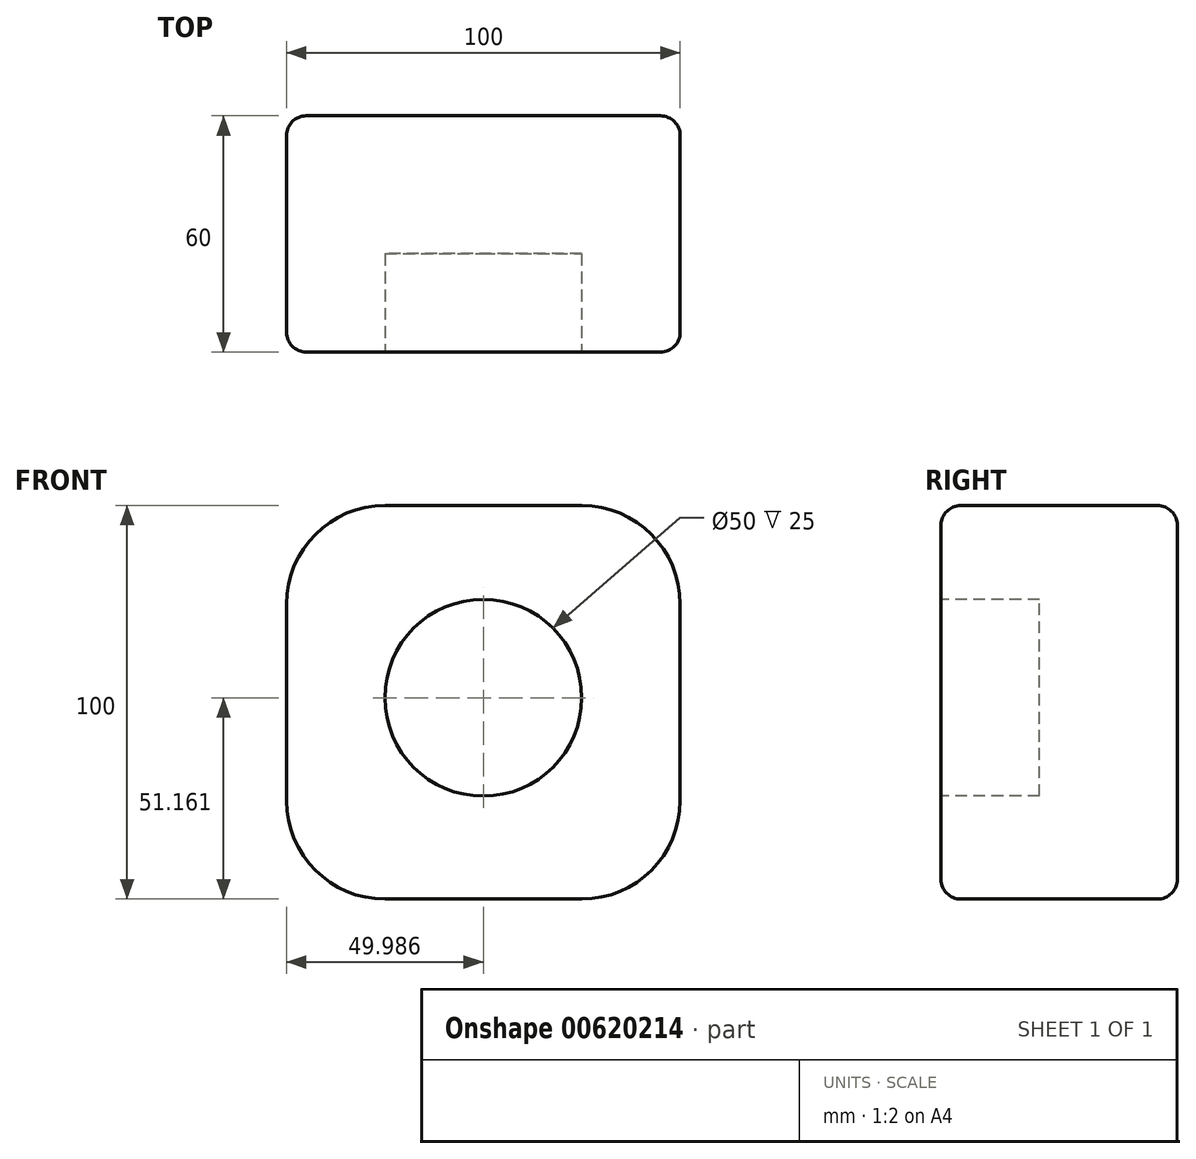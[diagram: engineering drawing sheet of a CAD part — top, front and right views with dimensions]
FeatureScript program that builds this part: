
annotation { "Feature Type Name" : "Feature", "Feature Type Description" : "" }
export const myFeature = defineFeature(function(context is Context, id is Id, definition is map)
    precondition{}
    {
        {
            var Q0;
            Q0=qCreatedBy(makeId("Front.planeOp"),FACE);
            var sketch = newSketch(context, id + "F0", { "sketchPlane" : qUnion([Q0])});
            skLineSegment(sketch, "E0.bottom", {"start": v(-40.91, 68.3) * mm, "end": v(9.09, 68.3) * mm});
            skLineSegment(sketch, "E0.top", {"start": v(-40.91, -31.7) * mm, "end": v(9.09, -31.7) * mm});
            skLineSegment(sketch, "E0.left", {"start": v(-65.91, 43.3) * mm, "end": v(-65.91, -6.7) * mm});
            skLineSegment(sketch, "E0.right", {"start": v(34.09, 43.3) * mm, "end": v(34.09, -6.7) * mm});
            skPoint(sketch, "E1.visualSharp", {"position": v(-65.91, 68.3) * mm});
            skArc(sketch, "E1.filletArc", {"start": v(-40.91, 68.3) * mm, "mid": v(-58.59, 60.98) * mm, "end": v(-65.91, 43.3) * mm});
            skPoint(sketch, "E2.visualSharp", {"position": v(34.09, -31.7) * mm});
            skArc(sketch, "E2.filletArc", {"start": v(9.09, -31.7) * mm, "mid": v(26.77, -24.37) * mm, "end": v(34.09, -6.7) * mm});
            skPoint(sketch, "E3.visualSharp", {"position": v(34.09, 68.3) * mm});
            skArc(sketch, "E3.filletArc", {"start": v(34.09, 43.3) * mm, "mid": v(26.77, 60.98) * mm, "end": v(9.09, 68.3) * mm});
            skPoint(sketch, "E4.visualSharp", {"position": v(-65.91, -31.7) * mm});
            skArc(sketch, "E4.filletArc", {"start": v(-65.91, -6.7) * mm, "mid": v(-58.59, -24.37) * mm, "end": v(-40.91, -31.7) * mm});
            skSolve(sketch);
        }
        {
            var Q0;
            Q0 = qSketchRegion(id + "F0", true);
            extrude(context, id + "F1", {"entities" : qUnion([Q0]), "depth" : 60 * mm, "offsetDistance" : 25 * mm});
        }
        {
            var Q0;
            Q0=makeQuery(id+"F1.opExtrude","CAP_FACE",FACE,{"disambiguationData":[OSD([sQuery(id+"F0.wireOp",EDGE,"E0.bottom"),sQuery(id+"F0.wireOp",EDGE,"E0.top"),sQuery(id+"F0.wireOp",EDGE,"E0.left"),sQuery(id+"F0.wireOp",EDGE,"E0.right"),sQuery(id+"F0.wireOp",EDGE,"E1.filletArc"),sQuery(id+"F0.wireOp",EDGE,"E2.filletArc"),sQuery(id+"F0.wireOp",EDGE,"E3.filletArc"),sQuery(id+"F0.wireOp",EDGE,"E4.filletArc")])],"isStart":false});
            var Q1;
            Q1=makeQuery(id+"F1.opExtrude","CAP_FACE",FACE,{"disambiguationData":[OSD([sQuery(id+"F0.wireOp",EDGE,"E0.bottom"),sQuery(id+"F0.wireOp",EDGE,"E0.top"),sQuery(id+"F0.wireOp",EDGE,"E0.left"),sQuery(id+"F0.wireOp",EDGE,"E0.right"),sQuery(id+"F0.wireOp",EDGE,"E1.filletArc"),sQuery(id+"F0.wireOp",EDGE,"E2.filletArc"),sQuery(id+"F0.wireOp",EDGE,"E3.filletArc"),sQuery(id+"F0.wireOp",EDGE,"E4.filletArc")])],"isStart":true});
            fillet(context, id + "F2", {"entities" : qUnion([Q0, Q1]), "radius" : 5 * mm, "tangentPropagation" : true, "allowEdgeOverflow" : false});
        }
        {
            var Q0;
            Q0=makeQuery(id+"F1.opExtrude","CAP_FACE",FACE,{"disambiguationData":[OSD([sQuery(id+"F0.wireOp",EDGE,"E0.bottom"),sQuery(id+"F0.wireOp",EDGE,"E0.top"),sQuery(id+"F0.wireOp",EDGE,"E0.left"),sQuery(id+"F0.wireOp",EDGE,"E0.right"),sQuery(id+"F0.wireOp",EDGE,"E1.filletArc"),sQuery(id+"F0.wireOp",EDGE,"E2.filletArc"),sQuery(id+"F0.wireOp",EDGE,"E3.filletArc"),sQuery(id+"F0.wireOp",EDGE,"E4.filletArc")])],"isStart":false});
            var sketch = newSketch(context, id + "F3", { "sketchPlane" : qUnion([Q0])});
            skCircle(sketch, "E5", {"center": v(-15.92, 19.47) * mm, "radius": 25 * mm});
            skSolve(sketch);
        }
        {
            var Q0;
            Q0=makeQuery(id+"F3.imprint","IMPRINT",FACE,{"disambiguationData":[TD([[makeQuery(id+"F3.imprint","IMPRINT",EDGE,{"derivedFrom":sQuery(id+"F3.wireOp",EDGE,"E5")}),1.0]])]});
            extrude(context, id + "F4", {"entities" : qUnion([Q0]), "operationType" : NewBodyOperationType.REMOVE, "oppositeDirection" : true, "depth" : 25 * mm, "offsetDistance" : 25 * mm});
        }
    });
